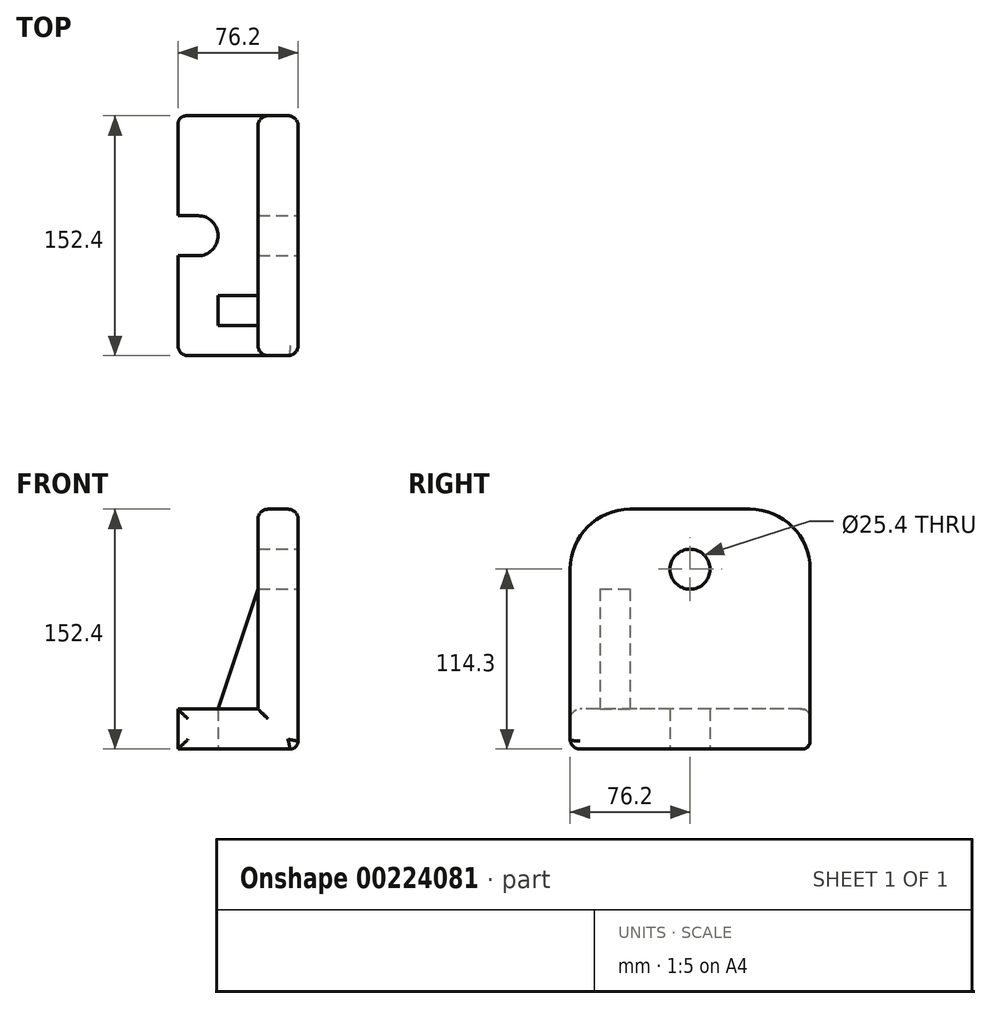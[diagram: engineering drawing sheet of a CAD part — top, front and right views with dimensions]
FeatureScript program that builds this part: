
annotation { "Feature Type Name" : "Feature", "Feature Type Description" : "" }
export const myFeature = defineFeature(function(context is Context, id is Id, definition is map)
    precondition{}
    {
        {
            var Q0;
            Q0=qCreatedBy(makeId("Front.planeOp"),FACE);
            var sketch = newSketch(context, id + "F0", { "sketchPlane" : qUnion([Q0])});
            skLineSegment(sketch, "E0", {"start": v(0, 0) * mm, "end": v(-76.2, 0) * mm});
            skLineSegment(sketch, "E1", {"start": v(0, 0) * mm, "end": v(0, 152.4) * mm});
            skLineSegment(sketch, "E2", {"start": v(-76.2, 0) * mm, "end": v(-76.2, 25.4) * mm});
            skLineSegment(sketch, "E3", {"start": v(-76.2, 25.4) * mm, "end": v(-25.4, 25.4) * mm});
            skLineSegment(sketch, "E4", {"start": v(0, 152.4) * mm, "end": v(-25.4, 152.4) * mm});
            skLineSegment(sketch, "E5", {"start": v(-25.4, 152.4) * mm, "end": v(-25.4, 25.4) * mm});
            skSolve(sketch);
        }
        {
            var Q0;
            Q0 = qSketchRegion(id + "F0", true);
            extrude(context, id + "F1", {"entities" : qUnion([Q0]), "endBound" : BoundingType.SYMMETRIC, "oppositeDirection" : true, "depth" : 152.4 * mm});
        }
        {
            var Q0;
            Q0=makeQuery(id+"F1.opExtrude","SWEPT_FACE",FACE,{"disambiguationData":[OSD([sQuery(id+"F0.wireOp",EDGE,"E1")])]});
            var sketch = newSketch(context, id + "F2", { "sketchPlane" : qUnion([Q0])});
            skLineSegment(sketch, "E6", {"start": v(0, 0) * mm, "end": v(0, 114.3) * mm, "construction": true});
            skCircle(sketch, "E7", {"center": v(0, 114.3) * mm, "radius": 12.7 * mm});
            skSolve(sketch);
        }
        {
            var Q0;
            Q0=makeQuery(id+"F2.imprint","IMPRINT",FACE,{"disambiguationData":[TD([[makeQuery(id+"F2.imprint","IMPRINT",EDGE,{"derivedFrom":sQuery(id+"F2.wireOp",EDGE,"E7")}),1.0]])]});
            extrude(context, id + "F3", {"entities" : qUnion([Q0]), "operationType" : NewBodyOperationType.REMOVE, "oppositeDirection" : true, "depth" : 53.1 * mm});
        }
        {
            var Q0;
            Q0=makeQuery(id+"F1.opExtrude","SWEPT_FACE",FACE,{"disambiguationData":[OSD([sQuery(id+"F0.wireOp",EDGE,"E0")])]});
            var sketch = newSketch(context, id + "F4", { "sketchPlane" : qUnion([Q0])});
            skArc(sketch, "E8", {"start": v(-63.5, -12.7) * mm, "mid": v(-50.8, 0) * mm, "end": v(-63.5, 12.7) * mm});
            skLineSegment(sketch, "E9", {"start": v(-63.5, -12.7) * mm, "end": v(-76.2, -12.7) * mm});
            skLineSegment(sketch, "E10", {"start": v(-63.5, 12.7) * mm, "end": v(-76.2, 12.7) * mm});
            skLineSegment(sketch, "E11", {"start": v(-76.2, 12.7) * mm, "end": v(-76.2, -12.7) * mm});
            skPoint(sketch, "E12", {"position": v(-76.2, 0) * mm});
            skSolve(sketch);
        }
        {
            var Q0;
            {var subQ0=sQuery(id+"F4.wireOp",EDGE,"E8");var subQ1=makeQuery(id+"F4.imprint","INTERSECT",VERTEX,{"derivedFrom":[subQ0,sQuery(id+"F4.wireOp",EDGE,"E10")]});Q0=makeQuery(id+"F4.imprint","IMPRINT",FACE,{"disambiguationData":[TD([[makeQuery(id+"F4.imprint","IMPRINT",EDGE,{"disambiguationData":[TD([[subQ1,-1.0]])],"derivedFrom":subQ0}),1.0]])]});}
            var Q1;
            {var subQ0=sQuery(id+"F4.wireOp",EDGE,"E10");Q1=makeQuery(id+"F4.imprint","IMPRINT",FACE,{"disambiguationData":[TD([[makeQuery(id+"F4.imprint","IMPRINT",EDGE,{"derivedFrom":subQ0}),1.0]])]});}
            var Q2;
            {var subQ0=sQuery(id+"F4.wireOp",EDGE,"E9");Q2=makeQuery(id+"F4.imprint","IMPRINT",FACE,{"disambiguationData":[TD([[makeQuery(id+"F4.imprint","IMPRINT",EDGE,{"derivedFrom":subQ0}),-1.0]])]});}
            extrude(context, id + "F5", {"entities" : qUnion([Q0, Q1, Q2]), "operationType" : NewBodyOperationType.REMOVE, "oppositeDirection" : true, "depth" : 34.8 * mm});
        }
        {
            var Q0;
            Q0=makeQuery(id+"F4.imprint","IMPRINT",FACE,{"disambiguationData":[TD([[makeQuery(id+"F4.imprint","IMPRINT",EDGE,{"derivedFrom":sQuery(id+"F4.wireOp",EDGE,"E8")}),1.0]])]});
            extrude(context, id + "F6", {"entities" : qUnion([Q0]), "operationType" : NewBodyOperationType.REMOVE, "oppositeDirection" : true, "depth" : 25.4 * mm});
        }
        {
            var Q0;
            Q0=makeQuery(id+"F1.opExtrude","CAP_EDGE",EDGE,{"disambiguationData":[OSD([sQuery(id+"F0.wireOp",EDGE,"E4")])],"isStart":false});
            var Q1;
            Q1=makeQuery(id+"F1.opExtrude","CAP_EDGE",EDGE,{"disambiguationData":[OSD([sQuery(id+"F0.wireOp",EDGE,"E4")])],"isStart":true});
            fillet(context, id + "F7", {"entities" : qUnion([Q0, Q1]), "radius" : 38.1 * mm, "tangentPropagation" : true, "allowEdgeOverflow" : false});
        }
        {
            var Q0;
            Q0=qCreatedBy(makeId("Front.planeOp"),FACE);
            cPlane(context, id + "F8", {"entities" : qUnion([Q0]), "cplaneType" : CPlaneType.OFFSET, "offset" : 44.45 * mm, "width" : 152.4 * mm, "height" : 152.4 * mm});
        }
        {
            var Q0;
            Q0=qCreatedBy(id+"F8.planeOp",FACE);
            var sketch = newSketch(context, id + "F9", { "sketchPlane" : qUnion([Q0])});
            skLineSegment(sketch, "E13.0", {"start": v(-50.8, 25.4) * mm, "end": v(-25.4, 25.4) * mm});
            skLineSegment(sketch, "E14.0", {"start": v(-25.4, 101.6) * mm, "end": v(-25.4, 25.4) * mm});
            skLineSegment(sketch, "E15", {"start": v(-50.8, 25.4) * mm, "end": v(-25.4, 101.6) * mm});
            skPoint(sketch, "E16.orphan", {"position": v(-76.2, 25.4) * mm});
            skPoint(sketch, "E17.orphan", {"position": v(-25.4, 114.3) * mm});
            skSolve(sketch);
        }
        {
            var Q0;
            {var subQ0=sQuery(id+"F9.wireOp",EDGE,"E14.0");Q0=makeQuery(id+"F9.imprint","IMPRINT",FACE,{"disambiguationData":[TD([[makeQuery(id+"F9.imprint","IMPRINT",EDGE,{"derivedFrom":subQ0}),-1.0]])]});}
            extrude(context, id + "F10", {"entities" : qUnion([Q0]), "operationType" : NewBodyOperationType.ADD, "depth" : 12.7 * mm});
        }
        {
            var Q0;
            Q0=makeQuery(id+"F9.imprint","IMPRINT",FACE,{"disambiguationData":[TD([[makeQuery(id+"F9.imprint","IMPRINT",EDGE,{"derivedFrom":sQuery(id+"F9.wireOp",EDGE,"E13.0")}),1.0]])]});
            extrude(context, id + "F11", {"entities" : qUnion([Q0]), "operationType" : NewBodyOperationType.ADD, "endBound" : BoundingType.SYMMETRIC, "depth" : 12.7 * mm});
        }
        {
            var Q0;
            Q0=makeQuery(id+"F1.opExtrude","CAP_EDGE",EDGE,{"disambiguationData":[OSD([sQuery(id+"F0.wireOp",EDGE,"E3")])],"isStart":true});
            var Q1;
            Q1=makeQuery(id+"F7.opFillet","BLEND_EDGE",EDGE,{"blendedFrom":[makeQuery(id+"F1.opExtrude","CAP_EDGE",EDGE,{"disambiguationData":[OSD([sQuery(id+"F0.wireOp",EDGE,"E4")])],"isStart":true}),makeQuery(id+"F1.opExtrude","SWEPT_FACE",FACE,{"disambiguationData":[OSD([sQuery(id+"F0.wireOp",EDGE,"E5")])]})],"blendedInto":[makeQuery(id+"F1.opExtrude","SWEPT_FACE",FACE,{"disambiguationData":[OSD([sQuery(id+"F0.wireOp",EDGE,"E5")])]})]});
            var Q2;
            Q2=makeQuery(id+"F1.opExtrude","CAP_EDGE",EDGE,{"disambiguationData":[OSD([sQuery(id+"F0.wireOp",EDGE,"E5")])],"isStart":true});
            var Q3;
            Q3=makeQuery(id+"F1.opExtrude","CAP_FACE",FACE,{"disambiguationData":[OSD([sQuery(id+"F0.wireOp",EDGE,"E0"),sQuery(id+"F0.wireOp",EDGE,"E1"),sQuery(id+"F0.wireOp",EDGE,"E2"),sQuery(id+"F0.wireOp",EDGE,"E3"),sQuery(id+"F0.wireOp",EDGE,"E4"),sQuery(id+"F0.wireOp",EDGE,"E5")])],"isStart":true});
            fillet(context, id + "F12", {"entities" : qUnion([Q0, Q1, Q2, Q3]), "radius" : 6.35 * mm, "tangentPropagation" : true, "allowEdgeOverflow" : false});
        }
        {
            var Q0;
            Q0=makeQuery(id+"F1.opExtrude","CAP_EDGE",EDGE,{"disambiguationData":[OSD([sQuery(id+"F0.wireOp",EDGE,"E3")])],"isStart":false});
            var Q1;
            Q1=makeQuery(id+"F1.opExtrude","CAP_FACE",FACE,{"disambiguationData":[OSD([sQuery(id+"F0.wireOp",EDGE,"E0"),sQuery(id+"F0.wireOp",EDGE,"E1"),sQuery(id+"F0.wireOp",EDGE,"E2"),sQuery(id+"F0.wireOp",EDGE,"E3"),sQuery(id+"F0.wireOp",EDGE,"E4"),sQuery(id+"F0.wireOp",EDGE,"E5")])],"isStart":false});
            fillet(context, id + "F13", {"entities" : qUnion([Q0, Q1]), "radius" : 5.08 * mm, "tangentPropagation" : true, "allowEdgeOverflow" : false});
        }
    });
